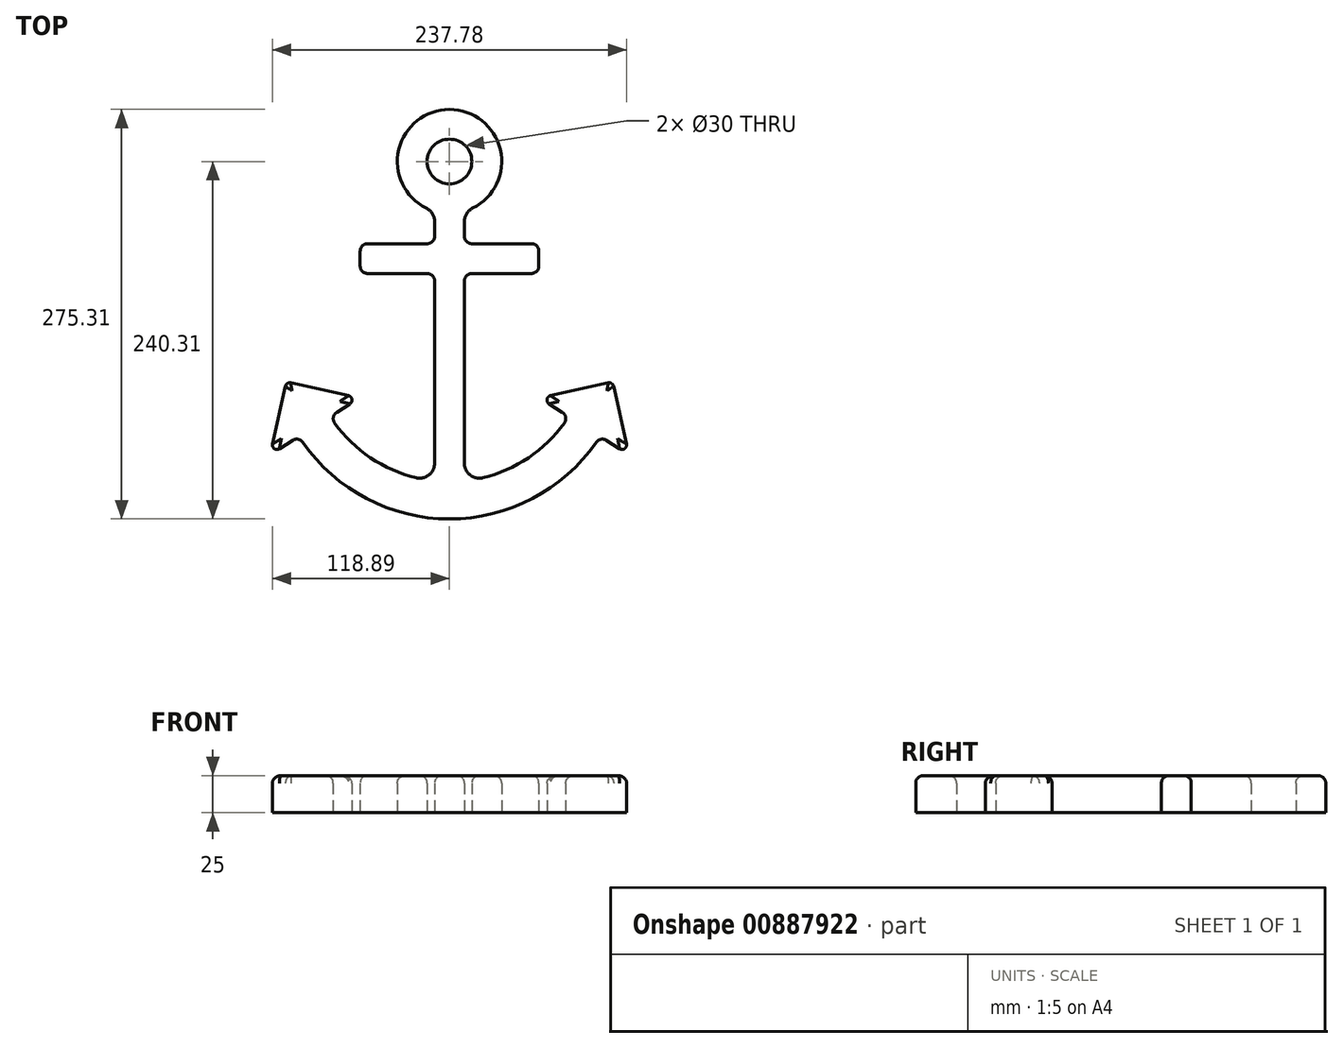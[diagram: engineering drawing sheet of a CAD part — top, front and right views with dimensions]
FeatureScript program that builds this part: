
annotation { "Feature Type Name" : "Feature", "Feature Type Description" : "" }
export const myFeature = defineFeature(function(context is Context, id is Id, definition is map)
    precondition{}
    {
        {
            var Q0;
            Q0=qCreatedBy(makeId("Top.planeOp"),FACE);
            var sketch = newSketch(context, id + "F0", { "sketchPlane" : qUnion([Q0])});
            skCircle(sketch, "E0", {"center": v(0, 0) * mm, "radius": 15 * mm});
            skArc(sketch, "E1", {"start": v(15.56, -31.35) * mm, "mid": v(0, 35) * mm, "end": v(-15.56, -31.35) * mm});
            skLineSegment(sketch, "E2.left", {"start": v(-10, -40.31) * mm, "end": v(-10, -50.31) * mm});
            skLineSegment(sketch, "E2.right", {"start": v(10, -40.31) * mm, "end": v(10, -50.31) * mm});
            skLineSegment(sketch, "E3.bottom", {"start": v(-55, -55.31) * mm, "end": v(-15, -55.31) * mm});
            skLineSegment(sketch, "E3.top", {"start": v(-55, -75.31) * mm, "end": v(-15, -75.31) * mm});
            skLineSegment(sketch, "E3.left", {"start": v(-60, -60.31) * mm, "end": v(-60, -70.31) * mm});
            skPoint(sketch, "E4.visualSharp", {"position": v(10, -33.54) * mm});
            skArc(sketch, "E4.filletArc", {"start": v(15.56, -31.35) * mm, "mid": v(11.5, -35.04) * mm, "end": v(10, -40.31) * mm});
            skPoint(sketch, "E5.visualSharp", {"position": v(-10, -33.54) * mm});
            skArc(sketch, "E5.filletArc", {"start": v(-10, -40.31) * mm, "mid": v(-11.5, -35.04) * mm, "end": v(-15.56, -31.35) * mm});
            skLineSegment(sketch, "E6.MirrorCS", {"start": v(55, -55.31) * mm, "end": v(15, -55.31) * mm});
            skLineSegment(sketch, "E7.MirrorCS", {"start": v(55, -75.31) * mm, "end": v(15, -75.31) * mm});
            skLineSegment(sketch, "E8.MirrorCS", {"start": v(60, -60.31) * mm, "end": v(60, -70.31) * mm});
            skArc(sketch, "E9", {"start": v(-77.16, -175.73) * mm, "mid": v(-53.07, -199.1) * mm, "end": v(-22.35, -212.64) * mm});
            skLineSegment(sketch, "E10.trimOffspring", {"start": v(-10, -80.31) * mm, "end": v(-10, -202.92) * mm});
            skLineSegment(sketch, "E11.trimOffspring", {"start": v(10, -80.31) * mm, "end": v(10, -202.92) * mm});
            skArc(sketch, "E12", {"start": v(-98.55, -188.78) * mm, "mid": v(0, -240.31) * mm, "end": v(98.55, -188.78) * mm});
            skPoint(sketch, "E13.visualSharp", {"position": v(-60, -55.31) * mm});
            skArc(sketch, "E13.filletArc", {"start": v(-55, -55.31) * mm, "mid": v(-58.54, -56.78) * mm, "end": v(-60, -60.31) * mm});
            skPoint(sketch, "E14.visualSharp", {"position": v(-60, -75.31) * mm});
            skArc(sketch, "E14.filletArc", {"start": v(-60, -70.31) * mm, "mid": v(-58.54, -73.85) * mm, "end": v(-55, -75.31) * mm});
            skPoint(sketch, "E15.visualSharp", {"position": v(60, -75.31) * mm});
            skArc(sketch, "E15.filletArc", {"start": v(55, -75.31) * mm, "mid": v(58.54, -73.85) * mm, "end": v(60, -70.31) * mm});
            skPoint(sketch, "E16.visualSharp", {"position": v(60, -55.31) * mm});
            skArc(sketch, "E16.filletArc", {"start": v(60, -60.31) * mm, "mid": v(58.54, -56.78) * mm, "end": v(55, -55.31) * mm});
            skLineSegment(sketch, "E17", {"start": v(-118.81, -189.93) * mm, "end": v(-110.2, -151.12) * mm});
            skLineSegment(sketch, "E18", {"start": v(-106.63, -148.84) * mm, "end": v(-67.82, -157.44) * mm});
            skLineSegment(sketch, "E19", {"start": v(-57.1, -254.02) * mm, "end": v(-101.2, -184.79) * mm, "construction": true});
            skPoint(sketch, "E20.visualSharp", {"position": v(-60.75, -159.01) * mm});
            skArc(sketch, "E20.filletArc", {"start": v(-66.85, -162.9) * mm, "mid": v(-65.51, -159.85) * mm, "end": v(-67.82, -157.44) * mm});
            skPoint(sketch, "E21.visualSharp", {"position": v(-109.56, -148.19) * mm});
            skArc(sketch, "E21.filletArc", {"start": v(-106.63, -148.84) * mm, "mid": v(-108.9, -149.24) * mm, "end": v(-110.2, -151.12) * mm});
            skPoint(sketch, "E22.visualSharp", {"position": v(-120.38, -197) * mm});
            skArc(sketch, "E22.filletArc", {"start": v(-118.81, -189.93) * mm, "mid": v(-117.6, -193.04) * mm, "end": v(-114.27, -193.11) * mm});
            skArc(sketch, "E23.trimOffspring", {"start": v(22.35, -212.64) * mm, "mid": v(53.07, -199.1) * mm, "end": v(77.16, -175.73) * mm});
            skPoint(sketch, "E24.visualSharp", {"position": v(10, -214.78) * mm});
            skArc(sketch, "E24.filletArc", {"start": v(10, -202.92) * mm, "mid": v(13.82, -210.78) * mm, "end": v(22.35, -212.64) * mm});
            skPoint(sketch, "E25.visualSharp", {"position": v(-10, -214.78) * mm});
            skArc(sketch, "E25.filletArc", {"start": v(-22.35, -212.64) * mm, "mid": v(-13.82, -210.78) * mm, "end": v(-10, -202.92) * mm});
            skLineSegment(sketch, "E26", {"start": v(-66.85, -162.9) * mm, "end": v(-75.79, -168.6) * mm});
            skLineSegment(sketch, "E27", {"start": v(-105.34, -187.42) * mm, "end": v(-114.27, -193.11) * mm});
            skLineSegment(sketch, "E28", {"start": v(-101.2, -184.79) * mm, "end": v(-80.12, -171.35) * mm, "construction": true});
            skArc(sketch, "E29.MirrorCS", {"start": v(106.63, -148.84) * mm, "mid": v(108.9, -149.24) * mm, "end": v(110.2, -151.12) * mm});
            skArc(sketch, "E30.MirrorCS", {"start": v(66.85, -162.9) * mm, "mid": v(65.51, -159.85) * mm, "end": v(67.82, -157.44) * mm});
            skLineSegment(sketch, "E31.MirrorCS", {"start": v(105.34, -187.42) * mm, "end": v(114.27, -193.11) * mm});
            skArc(sketch, "E32.MirrorCS", {"start": v(118.81, -189.93) * mm, "mid": v(117.6, -193.04) * mm, "end": v(114.27, -193.11) * mm});
            skLineSegment(sketch, "E33.MirrorCS", {"start": v(66.85, -162.9) * mm, "end": v(75.79, -168.6) * mm});
            skPoint(sketch, "E34.MirrorP", {"position": v(60.75, -159.01) * mm});
            skLineSegment(sketch, "E35.MirrorCS", {"start": v(118.81, -189.93) * mm, "end": v(110.2, -151.12) * mm});
            skPoint(sketch, "E36.MirrorP", {"position": v(109.56, -148.19) * mm});
            skLineSegment(sketch, "E37.MirrorCS", {"start": v(106.63, -148.84) * mm, "end": v(67.82, -157.44) * mm});
            skLineSegment(sketch, "E38.MirrorCS", {"start": v(101.2, -184.79) * mm, "end": v(80.12, -171.35) * mm, "construction": true});
            skPoint(sketch, "E39.MirrorP", {"position": v(120.38, -197) * mm});
            skPoint(sketch, "E40.visualSharp", {"position": v(-80.12, -171.35) * mm});
            skArc(sketch, "E40.filletArc", {"start": v(-75.79, -168.6) * mm, "mid": v(-78.01, -171.86) * mm, "end": v(-77.16, -175.73) * mm});
            skPoint(sketch, "E41.visualSharp", {"position": v(-101.2, -184.79) * mm});
            skArc(sketch, "E41.filletArc", {"start": v(-98.55, -188.78) * mm, "mid": v(-101.67, -186.73) * mm, "end": v(-105.34, -187.42) * mm});
            skPoint(sketch, "E42.visualSharp", {"position": v(101.2, -184.79) * mm});
            skArc(sketch, "E42.filletArc", {"start": v(105.34, -187.42) * mm, "mid": v(101.67, -186.73) * mm, "end": v(98.55, -188.78) * mm});
            skPoint(sketch, "E43.visualSharp", {"position": v(80.12, -171.35) * mm});
            skArc(sketch, "E43.filletArc", {"start": v(77.16, -175.73) * mm, "mid": v(78.01, -171.86) * mm, "end": v(75.79, -168.6) * mm});
            skPoint(sketch, "E44.visualSharp", {"position": v(-10, -55.31) * mm});
            skArc(sketch, "E44.filletArc", {"start": v(-15, -55.31) * mm, "mid": v(-11.46, -53.85) * mm, "end": v(-10, -50.31) * mm});
            skPoint(sketch, "E45.visualSharp", {"position": v(-10, -75.31) * mm});
            skArc(sketch, "E45.filletArc", {"start": v(-10, -80.31) * mm, "mid": v(-11.46, -76.78) * mm, "end": v(-15, -75.31) * mm});
            skPoint(sketch, "E46.visualSharp", {"position": v(10, -75.31) * mm});
            skArc(sketch, "E46.filletArc", {"start": v(15, -75.31) * mm, "mid": v(11.46, -76.78) * mm, "end": v(10, -80.31) * mm});
            skPoint(sketch, "E47.visualSharp", {"position": v(10, -55.31) * mm});
            skArc(sketch, "E47.filletArc", {"start": v(10, -50.31) * mm, "mid": v(11.46, -53.85) * mm, "end": v(15, -55.31) * mm});
            skSolve(sketch);
        }
        {
            var Q0;
            Q0=makeQuery(id+"F0.imprint","IMPRINT",FACE,{"disambiguationData":[TD([[makeQuery(id+"F0.imprint","IMPRINT",EDGE,{"derivedFrom":sQuery(id+"F0.wireOp",EDGE,"E0")}),-1.0]])]});
            var Q1;
            {var subQ6=sQuery(id+"F0.wireOp",EDGE,"E12");Q1=makeQuery(id+"F0.imprint","IMPRINT",FACE,{"disambiguationData":[TD([[makeQuery(id+"F0.imprint","IMPRINT",EDGE,{"derivedFrom":subQ6}),1.0]])]});}
            var Q2;
            Q2=makeQuery(id+"F0.imprint","IMPRINT",FACE,{"disambiguationData":[TD([[makeQuery(id+"F0.imprint","IMPRINT",EDGE,{"derivedFrom":sQuery(id+"F0.wireOp",EDGE,"E17")}),-1.0]])]});
            var Q3;
            Q3=makeQuery(id+"F0.imprint","IMPRINT",FACE,{"disambiguationData":[TD([[makeQuery(id+"F0.imprint","IMPRINT",EDGE,{"derivedFrom":sQuery(id+"F0.wireOp",EDGE,"288954a1-4b5b-4858-b1c7-edba4a30fe570.MirrorCS")}),-1.0]])]});
            extrude(context, id + "F1", {"entities" : qUnion([Q0, Q1, Q2, Q3]), "depth" : 25 * mm});
        }
        {
            var Q0;
            Q0=makeQuery(id+"F1.opExtrude","CAP_FACE",FACE,{"disambiguationData":[OSD([sQuery(id+"F0.wireOp",EDGE,"E0"),sQuery(id+"F0.wireOp",EDGE,"E1"),sQuery(id+"F0.wireOp",EDGE,"E2.left"),sQuery(id+"F0.wireOp",EDGE,"E2.right"),sQuery(id+"F0.wireOp",EDGE,"E3.bottom"),sQuery(id+"F0.wireOp",EDGE,"E3.top"),sQuery(id+"F0.wireOp",EDGE,"E3.left"),sQuery(id+"F0.wireOp",EDGE,"E4.filletArc"),sQuery(id+"F0.wireOp",EDGE,"E5.filletArc"),sQuery(id+"F0.wireOp",EDGE,"E6.MirrorCS"),sQuery(id+"F0.wireOp",EDGE,"E7.MirrorCS"),sQuery(id+"F0.wireOp",EDGE,"E8.MirrorCS"),sQuery(id+"F0.wireOp",EDGE,"E9"),sQuery(id+"F0.wireOp",EDGE,"E10.trimOffspring"),sQuery(id+"F0.wireOp",EDGE,"E11.trimOffspring"),sQuery(id+"F0.wireOp",EDGE,"E12"),sQuery(id+"F0.wireOp",EDGE,"E13.filletArc"),sQuery(id+"F0.wireOp",EDGE,"E14.filletArc"),sQuery(id+"F0.wireOp",EDGE,"E15.filletArc"),sQuery(id+"F0.wireOp",EDGE,"E16.filletArc"),sQuery(id+"F0.wireOp",EDGE,"E17"),sQuery(id+"F0.wireOp",EDGE,"E18"),sQuery(id+"F0.wireOp",EDGE,"E20.filletArc"),sQuery(id+"F0.wireOp",EDGE,"E21.filletArc"),sQuery(id+"F0.wireOp",EDGE,"E22.filletArc"),sQuery(id+"F0.wireOp",EDGE,"E23.trimOffspring"),sQuery(id+"F0.wireOp",EDGE,"E24.filletArc"),sQuery(id+"F0.wireOp",EDGE,"E25.filletArc"),sQuery(id+"F0.wireOp",EDGE,"E26"),sQuery(id+"F0.wireOp",EDGE,"E27"),sQuery(id+"F0.wireOp",EDGE,"E29.MirrorCS"),sQuery(id+"F0.wireOp",EDGE,"E30.MirrorCS"),sQuery(id+"F0.wireOp",EDGE,"E31.MirrorCS"),sQuery(id+"F0.wireOp",EDGE,"E32.MirrorCS"),sQuery(id+"F0.wireOp",EDGE,"E33.MirrorCS"),sQuery(id+"F0.wireOp",EDGE,"E35.MirrorCS"),sQuery(id+"F0.wireOp",EDGE,"E37.MirrorCS"),sQuery(id+"F0.wireOp",EDGE,"E40.filletArc"),sQuery(id+"F0.wireOp",EDGE,"E41.filletArc"),sQuery(id+"F0.wireOp",EDGE,"E42.filletArc"),sQuery(id+"F0.wireOp",EDGE,"E43.filletArc"),sQuery(id+"F0.wireOp",EDGE,"E44.filletArc"),sQuery(id+"F0.wireOp",EDGE,"E45.filletArc"),sQuery(id+"F0.wireOp",EDGE,"E46.filletArc"),sQuery(id+"F0.wireOp",EDGE,"E47.filletArc")])],"isStart":false});
            fillet(context, id + "F2", {"entities" : qUnion([Q0]), "radius" : 5 * mm, "tangentPropagation" : true, "allowEdgeOverflow" : false});
        }
    });
